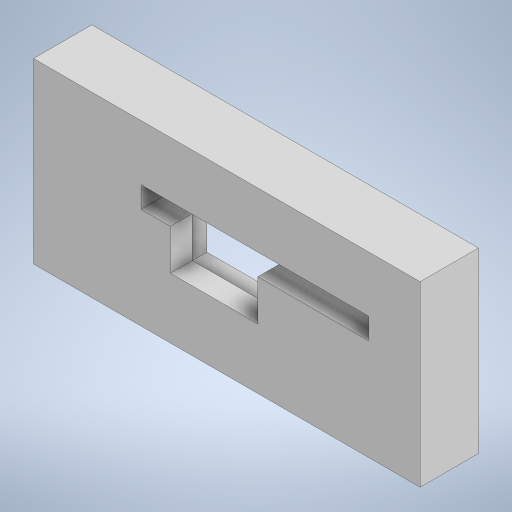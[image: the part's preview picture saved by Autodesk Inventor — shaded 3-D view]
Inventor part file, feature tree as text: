
AUTODESK INVENTOR PART (.ipt)
format: ipt  version: 2023 (Build 270158000, 158)  size: 606,720 bytes
history: native  units: in
note: dims shown in document units (in); Inventor stores cm internally (conversion verified against a paired STEP export)
features: extrude x17, sketch x15, fillet x2
ambient origin geometry x8: Origin, YZ Plane, XZ Plane, XY Plane, X Axis, Y Axis, Z Axis, Center Point
bodies: Solid1 (feature_tree)
feature tree (34):
  extrude  "Extrusion1"  Depth=7.0in
  extrude  "Extrusion2"  Depth=0.2in
  fillet  "Fillet1"  Radius=1.4in
  extrude  "Extrusion3"  Depth=0.125in
  extrude  "Extrusion4"  Depth=2.2875in
  extrude  "Extrusion5"  Depth=0.5437in
  sketch  "Sketch6"  dims[d13=0.75in d14=1.4in d15=0.0in]
  extrude  "Extrusion6"  Depth=1.4in TaperAngle=0.0deg
  extrude  "Extrusion9"  Depth=0.14in
  extrude  "Extrusion10"  Depth=0.1in
  extrude  "Extrusion11"  Depth=0.25in
  extrude  "Extrusion12"  Depth=0.15in
  extrude  "Extrusion13"  Depth=0.7in
  extrude  "Extrusion14"  Depth=0.1in
  extrude  "Extrusion15"  Depth=0.615in
  extrude  "Extrusion16"  Depth=1.1in
  fillet  "Fillet2"  Radius=0.21in
  extrude  "Extrusion17"  Depth=0.125in
  extrude  "Extrusion18"  Depth=0.125in
  extrude  "Extrusion19"  Depth=0.125in
  sketch  "Sketch1"  dims[d0=7.0in d1=4.5in]
  sketch  "Sketch2"  dims[d2=1.5in d3=0.0in d4=0.2in d5=1.4in d6=0.0in]
  sketch  "Sketch3"  dims[d7=0.125in d8=0.25in]
  sketch  "Sketch4"  dims[d9=0.25in d10=2.2875in]
  sketch  "Sketch5"  dims[d11=3.4125in d12=0.5437in]
  sketch  "Sketch8"  dims[d16=0.1in d17=0.14in]
  sketch  "Sketch9"  dims[d18=0.1in d19=0.275in]
  sketch  "Sketch10"  dims[d20=0.35in d21=0.25in]
  sketch  "Sketch11"  dims[d22=0.15in d23=0.15in]
  sketch  "Sketch12"  dims[d24=0.25in d25=0.7in]
  sketch  "Sketch13"  dims[d26=0.1in d27=0.1in]
  sketch  "Sketch14"  dims[d28=0.25in d29=0.615in]
  sketch  "Sketch15"  dims[d30=0.25in d31=1.1in d32=0.21in]
  sketch  "Sketch16"  dims[d33=0.3075in d34=0.5575in d35=1.65in d36=0.3075in d37=0.21in d38=0.5575in d39=2.1in d40=0.1in d41=0.1in d42=0.3in d43=0.1in d44=0.25in d45=0.615in d46=2.4in d47=0.11in d48=2.51in d49=0.5575in d50=0.1in d51=0.615in d52=0.175in d53=0.175in d54=0.1in d55=0.1in d56=0.25in d57=3.15in d58=0.1in d59=0.515in d60=0.05in d61=0.0in d62=0.1562in d63=0.1562in d64=0.2188in d65=0.2188in d66=0.2188in d67=0.2188in d68=0.2188in d69=0.2188in d70=0.625in d71=0.625in d72=0.625in d73=0.625in d74=0.8906in d76=2.25in d77=0.3in d78=0.3in d79=0.3in d80=0.3in d81=0.3in d82=0.625in d83=0.625in d84=0.625in d85=0.625in d86=1.0in d87=3.1in d88=3.1in d89=3.1in d90=3.1in d91=3.1in d92=1.0in d93=0.0in d97=0.4in d98=0.4in d99=0.4in d100=0.4in d101=0.4in d102=0.05in d103=0.0in d119=0.075in d120=0.075in d121=0.075in d122=0.075in d123=0.075in d124=0.0688in d125=0.0in d126=0.25in d127=0.275in d128=0.25in d129=0.25in d130=0.25in d131=2.1in d132=0.125in d133=0.0625in d134=0.05in d135=0.0in d136=0.6in d137=3.35in d139=0.3in d140=0.3155in d141=0.3157in d142=0.0375in d143=0.0in d144=2.0in d145=0.78in d146=0.0725in d147=0.3in d148=0.14in d149=0.1in d150=0.7in d151=0.2in d152=0.0in d153=0.075in d154=0.125in d155=0.0in d156=0.3in d157=2.5in d158=0.5in d159=0.25in d160=0.0in d161=0.5in d162=0.081in d163=0.0in d164=0.45in d165=0.6in d166=0.2in d167=0.2in d168=0.2in d169=0.075in d170=0.075in d171=0.075in d172=0.075in d173=0.2in d174=0.2in d175=0.2in d176=0.2in d177=0.075in d178=0.0in d179=0.125in d180=0.0375in d181=0.0375in d182=2.0in d183=0.5in d184=0.0in d185=0.0in d187=2.8in d188=5.0in d189=0.0in d190=5.0in d191=0.0in]
